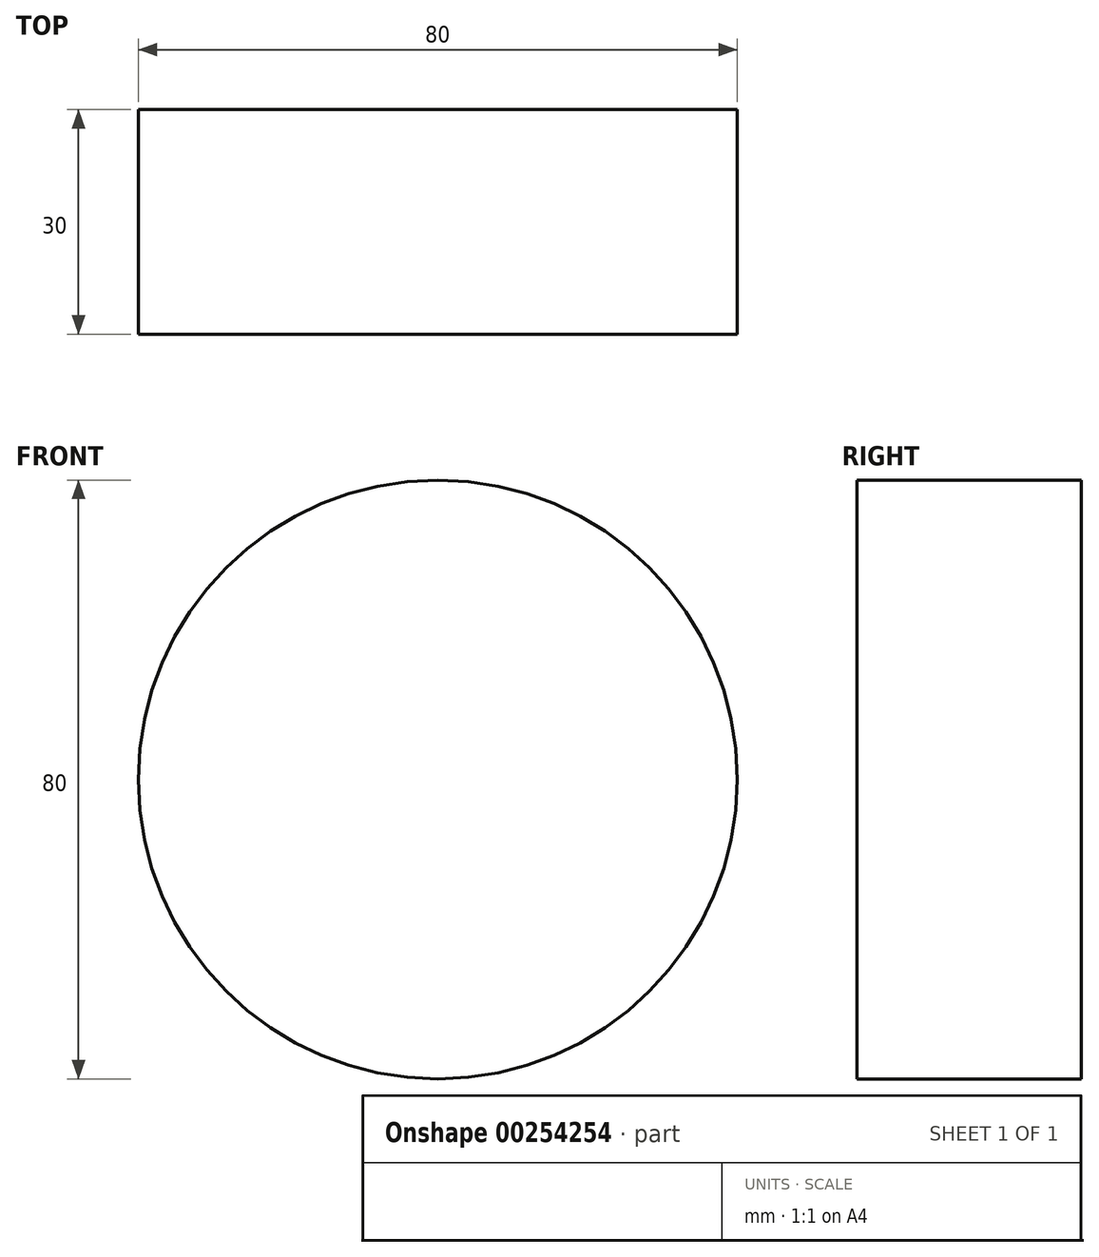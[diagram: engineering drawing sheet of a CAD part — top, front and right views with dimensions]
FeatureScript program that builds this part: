
annotation { "Feature Type Name" : "Feature", "Feature Type Description" : "" }
export const myFeature = defineFeature(function(context is Context, id is Id, definition is map)
    precondition{}
    {
        {
            var Q0;
            Q0=qCreatedBy(makeId("Front.planeOp"),FACE);
            var sketch = newSketch(context, id + "F0", { "sketchPlane" : qUnion([Q0])});
            skCircle(sketch, "E0", {"center": v(0, 0) * mm, "radius": 40 * mm});
            skSolve(sketch);
        }
        {
            var Q0;
            Q0=makeQuery(id+"F0.imprint","IMPRINT",FACE,{"disambiguationData":[TD([[makeQuery(id+"F0.imprint","IMPRINT",EDGE,{"derivedFrom":sQuery(id+"F0.wireOp",EDGE,"E0")}),1.0]])]});
            extrude(context, id + "F1", {"entities" : qUnion([Q0]), "depth" : 30 * mm});
        }
    });
